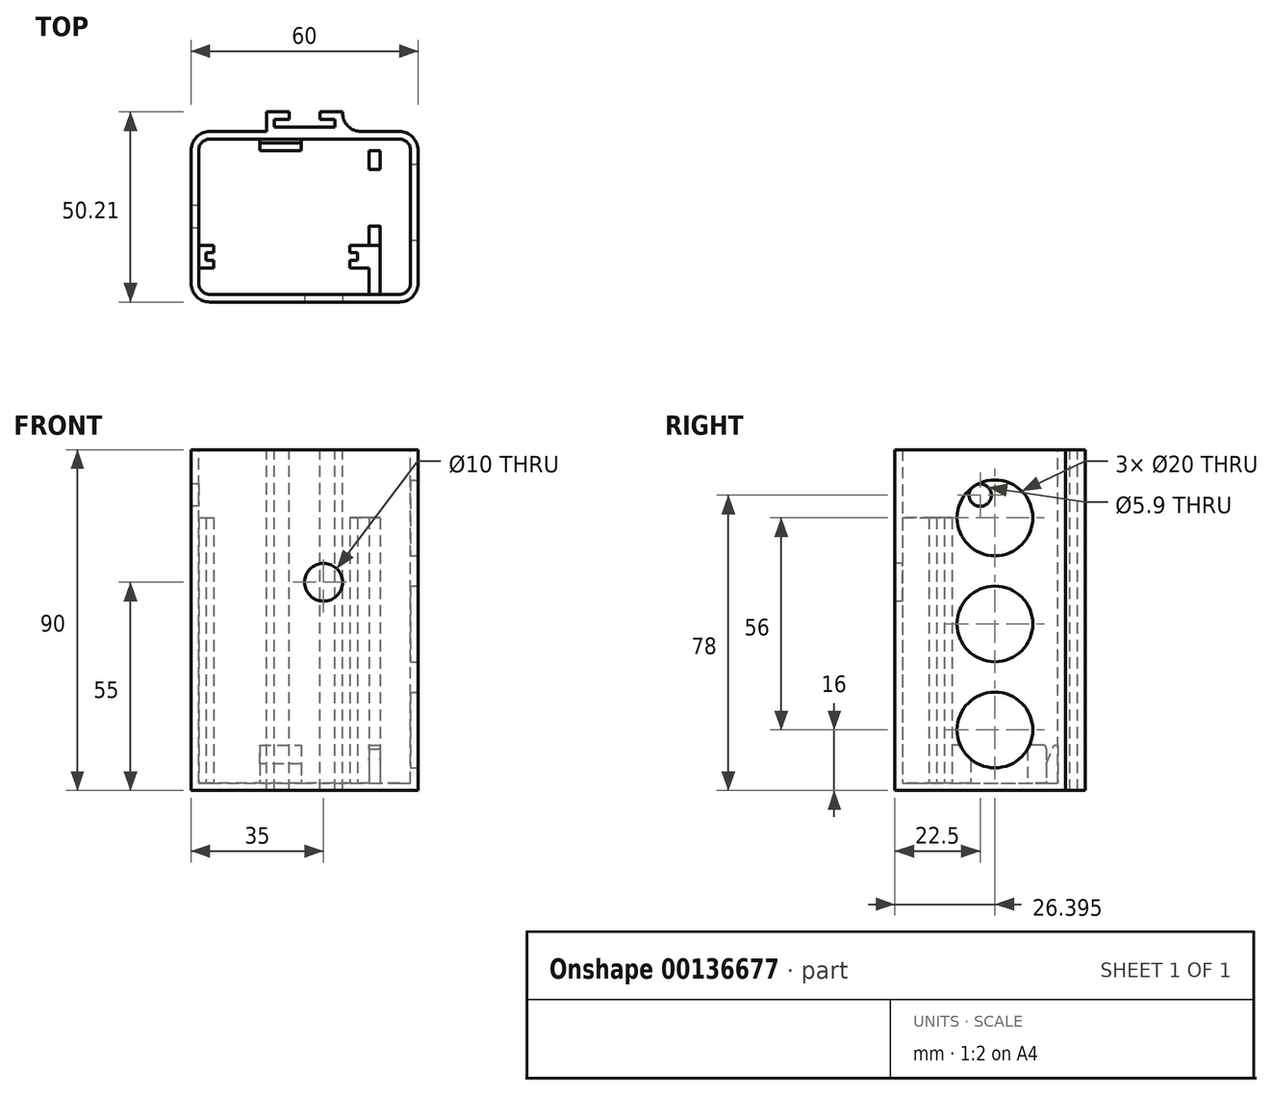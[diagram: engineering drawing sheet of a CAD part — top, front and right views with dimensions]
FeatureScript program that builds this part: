
annotation { "Feature Type Name" : "Feature", "Feature Type Description" : "" }
export const myFeature = defineFeature(function(context is Context, id is Id, definition is map)
    precondition{}
    {
        {
            var Q0;
            Q0=qCreatedBy(makeId("Top.planeOp"),FACE);
            var sketch = newSketch(context, id + "F0", { "sketchPlane" : qUnion([Q0])});
            skLineSegment(sketch, "E0", {"start": v(0, -66) * mm, "end": v(0, -116) * mm, "construction": true});
            skLineSegment(sketch, "E1", {"start": v(0, -116) * mm, "end": v(-35, -116) * mm});
            skLineSegment(sketch, "E2", {"start": v(-40, -111) * mm, "end": v(-40, -76) * mm});
            skLineSegment(sketch, "E3", {"start": v(0, -116) * mm, "end": v(15, -116) * mm});
            skLineSegment(sketch, "E4", {"start": v(20, -111) * mm, "end": v(20, -76) * mm});
            skLineSegment(sketch, "E5", {"start": v(-35, -71) * mm, "end": v(15, -71) * mm});
            skPoint(sketch, "E6.visualSharp", {"position": v(-40, -116) * mm});
            skArc(sketch, "E6.filletArc", {"start": v(-40, -111) * mm, "mid": v(-38.54, -114.54) * mm, "end": v(-35, -116) * mm});
            skPoint(sketch, "E7.visualSharp", {"position": v(20, -116) * mm});
            skArc(sketch, "E7.filletArc", {"start": v(15, -116) * mm, "mid": v(18.54, -114.54) * mm, "end": v(20, -111) * mm});
            skPoint(sketch, "E8.visualSharp", {"position": v(-40, -71) * mm});
            skArc(sketch, "E8.filletArc", {"start": v(-35, -71) * mm, "mid": v(-38.54, -72.46) * mm, "end": v(-40, -76) * mm});
            skPoint(sketch, "E9.visualSharp", {"position": v(20, -71) * mm});
            skArc(sketch, "E9.filletArc", {"start": v(20, -76) * mm, "mid": v(18.54, -72.46) * mm, "end": v(15, -71) * mm});
            skSolve(sketch);
        }
        {
            var Q0;
            Q0=makeQuery(id+"F0.imprint","IMPRINT",FACE,{"disambiguationData":[TD([[makeQuery(id+"F0.imprint","IMPRINT",EDGE,{"derivedFrom":sQuery(id+"F0.wireOp",EDGE,"E1")}),-1.0]])]});
            extrude(context, id + "F1", {"entities" : qUnion([Q0]), "depth" : 90 * mm});
        }
        {
            var Q0;
            Q0=makeQuery(id+"F1.opExtrude","CAP_FACE",FACE,{"disambiguationData":[OSD([sQuery(id+"F0.wireOp",EDGE,"kaPZJ7qW-dZjC-p6nc-pN5f-yqhQU7M3ZjwH"),sQuery(id+"F0.wireOp",EDGE,"8Wxh9i85-0xR2-3Pbf-Hzkg-k3FD4vluLN9F"),sQuery(id+"F0.wireOp",EDGE,"DCatT4Rc-aRkY-SHOm-8XJS-lDhrpB4yduI9"),sQuery(id+"F0.wireOp",EDGE,"1zJpH22H-yOzR-8Hfd-Y7F9-i502TLs9juBK"),sQuery(id+"F0.wireOp",EDGE,"dVugaCqK-bgcG-3lUM-ltb7-ybWCQGKNFEZq"),sQuery(id+"F0.wireOp",EDGE,"E1"),sQuery(id+"F0.wireOp",EDGE,"E2"),sQuery(id+"F0.wireOp",EDGE,"E3"),sQuery(id+"F0.wireOp",EDGE,"E4"),sQuery(id+"F0.wireOp",EDGE,"cf949580-c1d9-4f65-b7b1-19b60dd8008e.trimOffspring")])],"isStart":false});
            shell(context, id + "F2", {"entities" : qUnion([Q0]), "thickness" : 2 * mm});
        }
        {
            var Q0;
            Q0=makeQuery(id+"F1.opExtrude","CAP_FACE",FACE,{"disambiguationData":[OSD([sQuery(id+"F0.wireOp",EDGE,"kaPZJ7qW-dZjC-p6nc-pN5f-yqhQU7M3ZjwH"),sQuery(id+"F0.wireOp",EDGE,"8Wxh9i85-0xR2-3Pbf-Hzkg-k3FD4vluLN9F"),sQuery(id+"F0.wireOp",EDGE,"DCatT4Rc-aRkY-SHOm-8XJS-lDhrpB4yduI9"),sQuery(id+"F0.wireOp",EDGE,"1zJpH22H-yOzR-8Hfd-Y7F9-i502TLs9juBK"),sQuery(id+"F0.wireOp",EDGE,"dVugaCqK-bgcG-3lUM-ltb7-ybWCQGKNFEZq"),sQuery(id+"F0.wireOp",EDGE,"E1"),sQuery(id+"F0.wireOp",EDGE,"E2"),sQuery(id+"F0.wireOp",EDGE,"E3"),sQuery(id+"F0.wireOp",EDGE,"E4"),sQuery(id+"F0.wireOp",EDGE,"cf949580-c1d9-4f65-b7b1-19b60dd8008e.trimOffspring")])],"isStart":false});
            var sketch = newSketch(context, id + "F3", { "sketchPlane" : qUnion([Q0])});
            skLineSegment(sketch, "E10", {"start": v(-20, -71) * mm, "end": v(-10, -71) * mm});
            skLineSegment(sketch, "E11", {"start": v(-10, -71) * mm, "end": v(0, -71) * mm});
            skLineSegment(sketch, "E12", {"start": v(-20, -71) * mm, "end": v(-20, -65.8) * mm});
            skLineSegment(sketch, "E13", {"start": v(-20, -65.8) * mm, "end": v(-5.9, -65.8) * mm});
            skLineSegment(sketch, "E14", {"start": v(-5.9, -65.8) * mm, "end": v(-5.9, -67.8) * mm});
            skLineSegment(sketch, "E15", {"start": v(-5.9, -67.8) * mm, "end": v(-18, -67.8) * mm});
            skLineSegment(sketch, "E16", {"start": v(-18, -67.8) * mm, "end": v(-18, -69.8) * mm});
            skLineSegment(sketch, "E17", {"start": v(-18, -69.8) * mm, "end": v(-2, -69.8) * mm});
            skLineSegment(sketch, "E18", {"start": v(-2, -69.8) * mm, "end": v(-2, -67.8) * mm});
            skLineSegment(sketch, "E19", {"start": v(-2, -67.8) * mm, "end": v(-14.1, -67.8) * mm});
            skLineSegment(sketch, "E20", {"start": v(-14.1, -67.8) * mm, "end": v(-14.1, -65.8) * mm});
            skLineSegment(sketch, "E21", {"start": v(-14.1, -65.8) * mm, "end": v(0, -65.8) * mm});
            skLineSegment(sketch, "E22", {"start": v(0, -65.8) * mm, "end": v(0, -71) * mm});
            skLineSegment(sketch, "E23", {"start": v(-14.1, -65.8) * mm, "end": v(-5.9, -65.8) * mm, "construction": true});
            skLineSegment(sketch, "E24", {"start": v(-14.1, -67.8) * mm, "end": v(-5.9, -67.8) * mm, "construction": true});
            skLineSegment(sketch, "E25", {"start": v(-18, -69.8) * mm, "end": v(-20, -69.8) * mm, "construction": true});
            skLineSegment(sketch, "E26", {"start": v(-2, -69.8) * mm, "end": v(0, -69.8) * mm, "construction": true});
            skSolve(sketch);
        }
        {
            var Q0;
            Q0=makeQuery(id+"F3.imprint","IMPRINT",FACE,{"disambiguationData":[TD([[makeQuery(id+"F3.imprint","IMPRINT",EDGE,{"derivedFrom":sQuery(id+"F3.wireOp",EDGE,"E10")}),1.0]])]});
            var Q1;
            Q1=makeQuery(id+"F1.opExtrude","CAP_FACE",FACE,{"disambiguationData":[OSD([sQuery(id+"F0.wireOp",EDGE,"E1"),sQuery(id+"F0.wireOp",EDGE,"E2"),sQuery(id+"F0.wireOp",EDGE,"E3"),sQuery(id+"F0.wireOp",EDGE,"E4"),sQuery(id+"F0.wireOp",EDGE,"E5")])],"isStart":true});
            extrude(context, id + "F4", {"entities" : qUnion([Q0]), "operationType" : NewBodyOperationType.ADD, "endBound" : BoundingType.UP_TO_SURFACE, "oppositeDirection" : true, "endBoundEntityFace" : qUnion([Q1]), "depth" : 45 * mm});
        }
        {
            var Q0;
            Q0=makeQuery(id+"F1.opExtrude","SWEPT_FACE",FACE,{"disambiguationData":[OSD([sQuery(id+"F0.wireOp",EDGE,"E1"),sQuery(id+"F0.wireOp",EDGE,"E3")])]});
            var sketch = newSketch(context, id + "F5", { "sketchPlane" : qUnion([Q0])});
            skCircle(sketch, "E27", {"center": v(-5, 55) * mm, "radius": 5 * mm});
            skSolve(sketch);
        }
        {
            var Q0;
            Q0=qSketchRegion(id+"F5",true);
            extrude(context, id + "F6", {"entities" : qUnion([Q0]), "operationType" : NewBodyOperationType.REMOVE, "oppositeDirection" : true, "depth" : 25 * mm});
        }
        {
            var Q0;
            Q0=makeQuery(id+"F2.opShell","OFFSET_FACE",FACE,{"disambiguationData":[OSD([sQuery(id+"F0.wireOp",EDGE,"E1"),sQuery(id+"F0.wireOp",EDGE,"E2"),sQuery(id+"F0.wireOp",EDGE,"E3"),sQuery(id+"F0.wireOp",EDGE,"E4"),sQuery(id+"F0.wireOp",EDGE,"E5"),sQuery(id+"F0.wireOp",EDGE,"E6.filletArc"),sQuery(id+"F0.wireOp",EDGE,"E7.filletArc"),sQuery(id+"F0.wireOp",EDGE,"E8.filletArc"),sQuery(id+"F0.wireOp",EDGE,"E9.filletArc")])]});
            var sketch = newSketch(context, id + "F7", { "sketchPlane" : qUnion([Q0])});
            skLineSegment(sketch, "E28.bottom", {"start": v(-38, -76) * mm, "end": v(7, -76) * mm, "construction": true});
            skLineSegment(sketch, "E28.top", {"start": v(-38, -101) * mm, "end": v(7, -101) * mm, "construction": true});
            skLineSegment(sketch, "E28.left", {"start": v(-38, -76) * mm, "end": v(-38, -101) * mm, "construction": true});
            skLineSegment(sketch, "E28.right", {"start": v(7, -76) * mm, "end": v(7, -81) * mm, "construction": true});
            skLineSegment(sketch, "E29.bottom", {"start": v(-21.85, -76) * mm, "end": v(-10.88, -76) * mm});
            skLineSegment(sketch, "E29.top", {"start": v(-21.85, -73) * mm, "end": v(-10.88, -73) * mm});
            skLineSegment(sketch, "E29.left", {"start": v(-21.85, -76) * mm, "end": v(-21.85, -73) * mm});
            skLineSegment(sketch, "E29.right", {"start": v(-10.88, -76) * mm, "end": v(-10.88, -73) * mm});
            skLineSegment(sketch, "E30.bottom", {"start": v(7, -76) * mm, "end": v(10, -76) * mm});
            skLineSegment(sketch, "E30.top", {"start": v(7, -101) * mm, "end": v(10, -101) * mm});
            skLineSegment(sketch, "E30.left", {"start": v(7, -76) * mm, "end": v(7, -81) * mm});
            skLineSegment(sketch, "E30.right", {"start": v(10, -76) * mm, "end": v(10, -81) * mm});
            skLineSegment(sketch, "E31", {"start": v(7, -81) * mm, "end": v(10, -81) * mm});
            skLineSegment(sketch, "E32", {"start": v(7, -96) * mm, "end": v(10, -96) * mm});
            skLineSegment(sketch, "E33.trimOffspring", {"start": v(7, -96) * mm, "end": v(7, -101) * mm, "construction": true});
            skLineSegment(sketch, "E34.trimOffspring", {"start": v(10, -96) * mm, "end": v(10, -101) * mm});
            skLineSegment(sketch, "E35.trimOffspring", {"start": v(7, -96) * mm, "end": v(7, -101) * mm});
            skSolve(sketch);
        }
        {
            var Q0;
            Q0=qSketchRegion(id+"F7",true);
            extrude(context, id + "F8", {"entities" : qUnion([Q0]), "operationType" : NewBodyOperationType.ADD, "depth" : 10 * mm});
        }
        {
            var Q0;
            Q0=makeQuery(id+"F2.opShell","OFFSET_FACE",FACE,{"disambiguationData":[OSD([sQuery(id+"F0.wireOp",EDGE,"E1"),sQuery(id+"F0.wireOp",EDGE,"E2"),sQuery(id+"F0.wireOp",EDGE,"E3"),sQuery(id+"F0.wireOp",EDGE,"E4"),sQuery(id+"F0.wireOp",EDGE,"E5"),sQuery(id+"F0.wireOp",EDGE,"E6.filletArc"),sQuery(id+"F0.wireOp",EDGE,"E7.filletArc"),sQuery(id+"F0.wireOp",EDGE,"E8.filletArc"),sQuery(id+"F0.wireOp",EDGE,"E9.filletArc")])]});
            var sketch = newSketch(context, id + "F9", { "sketchPlane" : qUnion([Q0])});
            skLineSegment(sketch, "E36", {"start": v(-38, -101) * mm, "end": v(-34, -101) * mm});
            skLineSegment(sketch, "E37", {"start": v(-34, -101) * mm, "end": v(-34, -103) * mm});
            skLineSegment(sketch, "E38", {"start": v(-34, -103) * mm, "end": v(-36, -103) * mm});
            skLineSegment(sketch, "E39", {"start": v(-36, -103) * mm, "end": v(-36, -105) * mm});
            skLineSegment(sketch, "E40", {"start": v(-36, -105) * mm, "end": v(-34, -105) * mm});
            skLineSegment(sketch, "E41", {"start": v(-34, -105) * mm, "end": v(-34, -107) * mm});
            skLineSegment(sketch, "E42", {"start": v(-34, -107) * mm, "end": v(-38, -107) * mm});
            skLineSegment(sketch, "E43", {"start": v(-38, -107) * mm, "end": v(-38, -101) * mm});
            skLineSegment(sketch, "E44", {"start": v(-34, -101) * mm, "end": v(2, -101) * mm, "construction": true});
            skLineSegment(sketch, "E45", {"start": v(2, -101) * mm, "end": v(7, -101) * mm});
            skLineSegment(sketch, "E46", {"start": v(10, -101) * mm, "end": v(10, -107) * mm});
            skLineSegment(sketch, "E47", {"start": v(7, -107) * mm, "end": v(2, -107) * mm});
            skLineSegment(sketch, "E48", {"start": v(2, -107) * mm, "end": v(2, -105) * mm});
            skLineSegment(sketch, "E49", {"start": v(2, -105) * mm, "end": v(4, -105) * mm});
            skLineSegment(sketch, "E50", {"start": v(4, -105) * mm, "end": v(4, -103) * mm});
            skLineSegment(sketch, "E51", {"start": v(4, -103) * mm, "end": v(2, -103) * mm});
            skLineSegment(sketch, "E52", {"start": v(2, -103) * mm, "end": v(2, -101) * mm});
            skLineSegment(sketch, "E53", {"start": v(10, -107) * mm, "end": v(10, -114) * mm});
            skLineSegment(sketch, "E54", {"start": v(10, -114) * mm, "end": v(7, -114) * mm});
            skLineSegment(sketch, "E55", {"start": v(7, -114) * mm, "end": v(7, -107) * mm});
            skLineSegment(sketch, "E56", {"start": v(7, -101) * mm, "end": v(10, -101) * mm});
            skSolve(sketch);
        }
        {
            var Q0;
            Q0=qSketchRegion(id+"F9",true);
            var Q1;
            Q1=makeQuery(id+"F4.boolean.opBoolean","MERGE",FACE,{"derivedFrom":[makeQuery(id+"F1.opExtrude","CAP_FACE",FACE,{"disambiguationData":[OSD([sQuery(id+"F0.wireOp",EDGE,"E1"),sQuery(id+"F0.wireOp",EDGE,"E2"),sQuery(id+"F0.wireOp",EDGE,"E3"),sQuery(id+"F0.wireOp",EDGE,"E4"),sQuery(id+"F0.wireOp",EDGE,"E5"),sQuery(id+"F0.wireOp",EDGE,"E6.filletArc"),sQuery(id+"F0.wireOp",EDGE,"E7.filletArc"),sQuery(id+"F0.wireOp",EDGE,"E8.filletArc"),sQuery(id+"F0.wireOp",EDGE,"E9.filletArc")])],"isStart":false}),makeQuery(id+"F4.opExtrude","CAP_FACE",FACE,{"disambiguationData":[OSD([sQuery(id+"F3.wireOp",EDGE,"E10"),sQuery(id+"F3.wireOp",EDGE,"E11"),sQuery(id+"F3.wireOp",EDGE,"E12"),sQuery(id+"F3.wireOp",EDGE,"E13"),sQuery(id+"F3.wireOp",EDGE,"E14"),sQuery(id+"F3.wireOp",EDGE,"E15"),sQuery(id+"F3.wireOp",EDGE,"E16"),sQuery(id+"F3.wireOp",EDGE,"E17"),sQuery(id+"F3.wireOp",EDGE,"E18"),sQuery(id+"F3.wireOp",EDGE,"E19"),sQuery(id+"F3.wireOp",EDGE,"E20"),sQuery(id+"F3.wireOp",EDGE,"E21"),sQuery(id+"F3.wireOp",EDGE,"E22")])],"isStart":true})]});
            extrude(context, id + "F10", {"entities" : qUnion([Q0]), "operationType" : NewBodyOperationType.ADD, "endBoundEntityFace" : qUnion([Q1]), "depth" : 70 * mm});
        }
        {
            var Q0;
            Q0=makeQuery(id+"F1.opExtrude","SWEPT_FACE",FACE,{"disambiguationData":[OSD([sQuery(id+"F0.wireOp",EDGE,"E4")])]});
            var sketch = newSketch(context, id + "F11", { "sketchPlane" : qUnion([Q0])});
            skCircle(sketch, "E57", {"center": v(-89.6, 72) * mm, "radius": 13.5 * mm, "construction": true});
            skLineSegment(sketch, "E58", {"start": v(-89.6, 72) * mm, "end": v(-89.6, 90) * mm, "construction": true});
            skLineSegment(sketch, "E59", {"start": v(-89.6, 72) * mm, "end": v(-89.6, 44) * mm, "construction": true});
            skLineSegment(sketch, "E60", {"start": v(-89.6, 44) * mm, "end": v(-89.6, 16) * mm, "construction": true});
            skCircle(sketch, "E61", {"center": v(-89.6, 44) * mm, "radius": 13.5 * mm, "construction": true});
            skCircle(sketch, "E62", {"center": v(-89.6, 16) * mm, "radius": 13.5 * mm, "construction": true});
            skCircle(sketch, "E63", {"center": v(-89.6, 72) * mm, "radius": 10 * mm});
            skCircle(sketch, "E64", {"center": v(-89.6, 44) * mm, "radius": 10 * mm});
            skCircle(sketch, "E65", {"center": v(-89.6, 16) * mm, "radius": 10 * mm});
            skSolve(sketch);
        }
        {
            var Q0;
            Q0=qSketchRegion(id+"F11",true);
            extrude(context, id + "F12", {"entities" : qUnion([Q0]), "operationType" : NewBodyOperationType.REMOVE, "oppositeDirection" : true, "depth" : 20 * mm});
        }
        {
            var Q0;
            Q0=makeQuery(id+"F4.opExtrude","SWEPT_EDGE",EDGE,{"disambiguationData":[OSD([sQuery(id+"F0.wireOp",EDGE,"E5"),sQuery(id+"F3.wireOp",EDGE,"E11"),sQuery(id+"F3.wireOp",EDGE,"E22")])]});
            var Q1;
            Q1=makeQuery(id+"F4.opExtrude","SWEPT_EDGE",EDGE,{"disambiguationData":[OSD([sQuery(id+"F0.wireOp",EDGE,"E5"),sQuery(id+"F3.wireOp",EDGE,"E10"),sQuery(id+"F3.wireOp",EDGE,"E12")])]});
            fillet(context, id + "F13", {"entities" : qUnion([Q0, Q1]), "radius" : 5 * mm, "tangentPropagation" : true, "allowEdgeOverflow" : false});
        }
        {
            var Q0;
            Q0=makeQuery(id+"F8.opExtrude","CAP_EDGE",EDGE,{"disambiguationData":[OSD([sQuery(id+"F7.wireOp",EDGE,"E29.bottom")])],"isStart":false});
            chamfer(context, id + "F14", {"entities" : qUnion([Q0]), "chamferType" : ChamferType.TWO_OFFSETS, "width1" : 2 * mm, "oppositeDirection" : false, "width2" : 5 * mm, "tangentPropagation" : true});
        }
        {
            var Q0;
            Q0=makeQuery(id+"F10.opExtrude","CAP_EDGE",EDGE,{"disambiguationData":[OSD([sQuery(id+"F9.wireOp",EDGE,"DjuyDg0v-B8Ic-I2eo-ft4Z-qBdWAiaMYZ0s")])],"isStart":false});
            var Q1;
            Q1=makeQuery(id+"F12.boolean.opBoolean","INTERSECT",EDGE,{"derivedFrom":[makeQuery(id+"F8.opExtrude","CAP_FACE",FACE,{"disambiguationData":[OSD([sQuery(id+"F7.wireOp",EDGE,"E30.bottom"),sQuery(id+"F7.wireOp",EDGE,"E30.left"),sQuery(id+"F7.wireOp",EDGE,"E30.right"),sQuery(id+"F7.wireOp",EDGE,"E31")])],"isStart":false}),makeQuery(id+"F12.opExtrude","SWEPT_FACE",FACE,{"disambiguationData":[OSD([sQuery(id+"F11.wireOp",EDGE,"E65")])]})]});
            var Q2;
            Q2=makeQuery(id+"F8.opExtrude","CAP_EDGE",EDGE,{"disambiguationData":[OSD([sQuery(id+"F7.wireOp",EDGE,"E30.bottom")])],"isStart":false});
            var Q3;
            Q3=makeQuery(id+"F12.boolean.opBoolean","INTERSECT",EDGE,{"derivedFrom":[makeQuery(id+"F8.opExtrude","CAP_FACE",FACE,{"disambiguationData":[OSD([sQuery(id+"F7.wireOp",EDGE,"E30.top"),sQuery(id+"F7.wireOp",EDGE,"E32"),sQuery(id+"F7.wireOp",EDGE,"E34.trimOffspring"),sQuery(id+"F7.wireOp",EDGE,"E35.trimOffspring")])],"isStart":false}),makeQuery(id+"F12.opExtrude","SWEPT_FACE",FACE,{"disambiguationData":[OSD([sQuery(id+"F11.wireOp",EDGE,"E65")])]})]});
            var Q4;
            Q4=makeQuery(id+"F12.boolean.opBoolean","INTERSECT",EDGE,{"derivedFrom":[makeQuery(id+"F8.opExtrude","SWEPT_FACE",FACE,{"disambiguationData":[OSD([sQuery(id+"F7.wireOp",EDGE,"E32")])]}),makeQuery(id+"F12.opExtrude","SWEPT_FACE",FACE,{"disambiguationData":[OSD([sQuery(id+"F11.wireOp",EDGE,"E65")])]})]});
            fillet(context, id + "F15", {"entities" : qUnion([Q0, Q1, Q2, Q3, Q4]), "radius" : 1 * mm, "tangentPropagation" : true, "allowEdgeOverflow" : false});
        }
        {
            var Q0;
            Q0=makeQuery(id+"F1.opExtrude","SWEPT_FACE",FACE,{"disambiguationData":[OSD([sQuery(id+"F0.wireOp",EDGE,"E2")])]});
            var sketch = newSketch(context, id + "F16", { "sketchPlane" : qUnion([Q0])});
            skCircle(sketch, "E66", {"center": v(93.5, 78) * mm, "radius": 2.95 * mm});
            skSolve(sketch);
        }
        {
            var Q0;
            Q0=qSketchRegion(id+"F16",true);
            extrude(context, id + "F17", {"entities" : qUnion([Q0]), "operationType" : NewBodyOperationType.REMOVE, "oppositeDirection" : true, "depth" : 25 * mm});
        }
    });
